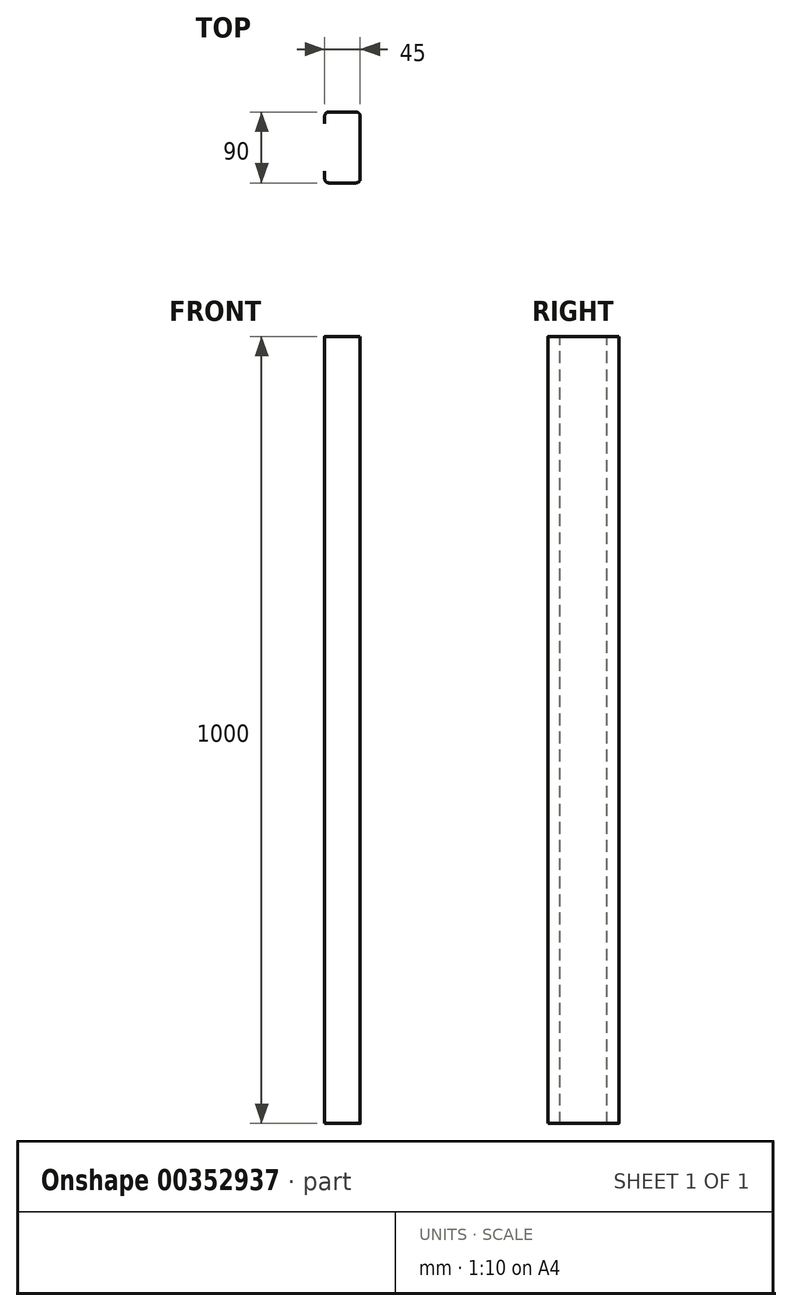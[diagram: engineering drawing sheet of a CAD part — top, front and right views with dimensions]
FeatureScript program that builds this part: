
annotation { "Feature Type Name" : "Feature", "Feature Type Description" : "" }
export const myFeature = defineFeature(function(context is Context, id is Id, definition is map)
    precondition{}
    {
        {
            var Q0;
            Q0=qCreatedBy(makeId("Top.planeOp"),FACE);
            var sketch = newSketch(context, id + "F0", { "sketchPlane" : qUnion([Q0])});
            skLineSegment(sketch, "E0.bottom", {"start": v(22.5, -40) * mm, "end": v(22.5, 40) * mm});
            skLineSegment(sketch, "E0.top", {"start": v(-22.5, -40) * mm, "end": v(-22.5, -30) * mm});
            skLineSegment(sketch, "E0.left", {"start": v(17.5, -45) * mm, "end": v(-17.5, -45) * mm});
            skLineSegment(sketch, "E0.right", {"start": v(17.5, 45) * mm, "end": v(-17.5, 45) * mm});
            skPoint(sketch, "E0.middle", {"position": v(0, 0) * mm});
            skLineSegment(sketch, "E1", {"start": v(-22.5, 30) * mm, "end": v(-22.5, 40) * mm});
            skPoint(sketch, "E2.visualSharp", {"position": v(-22.5, 45) * mm});
            skArc(sketch, "E2.filletArc", {"start": v(-17.5, 45) * mm, "mid": v(-21.04, 43.54) * mm, "end": v(-22.5, 40) * mm});
            skPoint(sketch, "E3.visualSharp", {"position": v(22.5, 45) * mm});
            skArc(sketch, "E3.filletArc", {"start": v(22.5, 40) * mm, "mid": v(21.04, 43.54) * mm, "end": v(17.5, 45) * mm});
            skPoint(sketch, "E4.visualSharp", {"position": v(22.5, -45) * mm});
            skArc(sketch, "E4.filletArc", {"start": v(17.5, -45) * mm, "mid": v(21.04, -43.54) * mm, "end": v(22.5, -40) * mm});
            skPoint(sketch, "E5.visualSharp", {"position": v(-22.5, -45) * mm});
            skArc(sketch, "E5.filletArc", {"start": v(-22.5, -40) * mm, "mid": v(-21.04, -43.54) * mm, "end": v(-17.5, -45) * mm});
            skSolve(sketch);
        }
        {
            var Q0;
            Q0=qConstructionFilter(qBodyType(qCreatedBy(id+"F0",EDGE),BodyType.WIRE),ConstructionObject.NO);
            extrude(context, id + "F1", {"bodyType" : ToolBodyType.SURFACE, "surfaceEntities" : qUnion([Q0]), "depth" : 1000 * mm});
        }
    });
